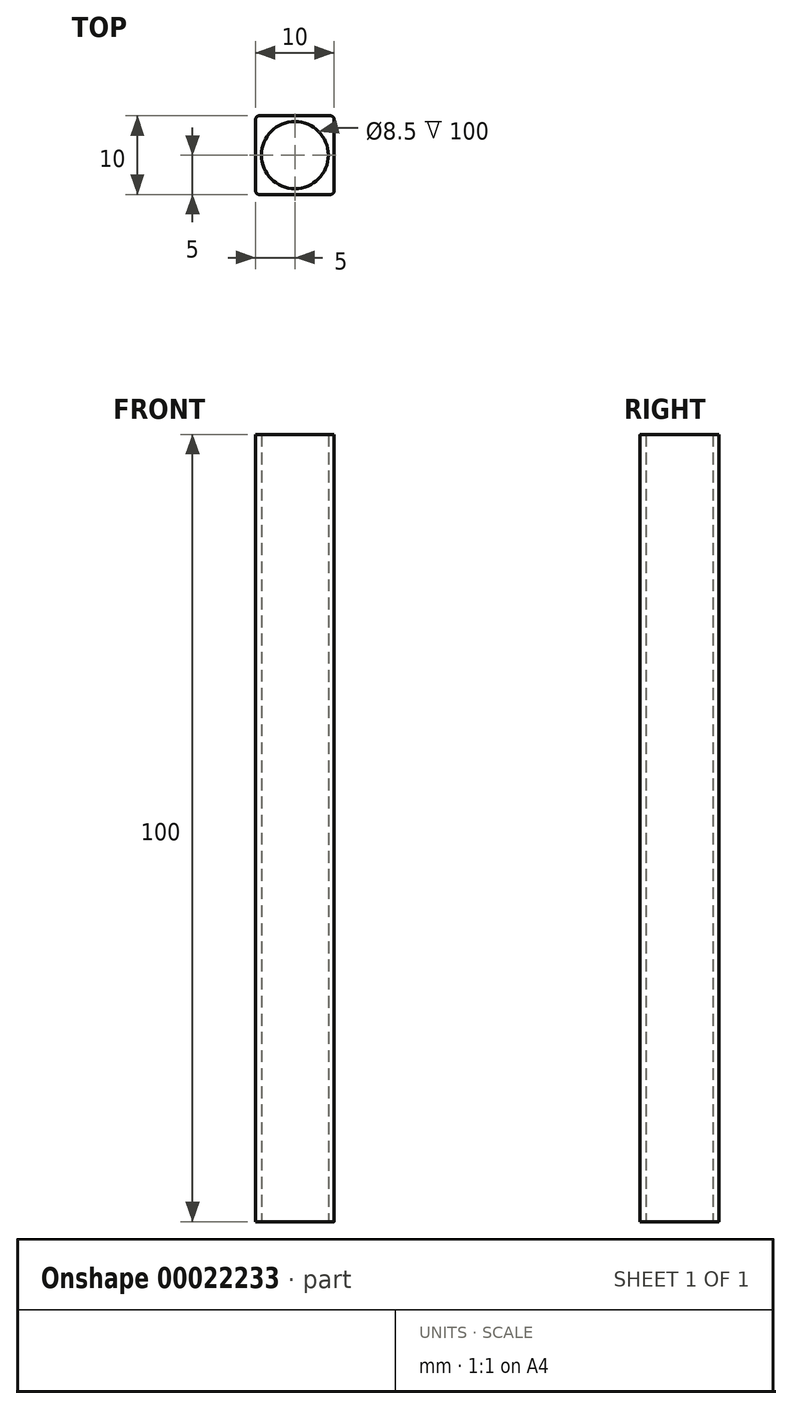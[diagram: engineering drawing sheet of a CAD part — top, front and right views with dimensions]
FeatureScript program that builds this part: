
annotation { "Feature Type Name" : "Feature", "Feature Type Description" : "" }
export const myFeature = defineFeature(function(context is Context, id is Id, definition is map)
    precondition{}
    {
        {
            var Q0;
            Q0=qCreatedBy(makeId("Top.planeOp"),FACE);
            var sketch = newSketch(context, id + "F0", { "sketchPlane" : qUnion([Q0])});
            skLineSegment(sketch, "E0.rect.bottom", {"start": v(-4.5, 5) * mm, "end": v(4.5, 5) * mm});
            skLineSegment(sketch, "E0.rect.top", {"start": v(-4.5, -5) * mm, "end": v(4.5, -5) * mm});
            skLineSegment(sketch, "E0.rect.left", {"start": v(-5, 4.5) * mm, "end": v(-5, -4.5) * mm});
            skLineSegment(sketch, "E0.rect.right", {"start": v(5, 4.5) * mm, "end": v(5, -4.5) * mm});
            skPoint(sketch, "E0.rect.middle", {"position": v(0, 0) * mm});
            skCircle(sketch, "E1", {"center": v(0, 0) * mm, "radius": 4.25 * mm});
            skPoint(sketch, "E2.visualSharp", {"position": v(-5, 5) * mm});
            skArc(sketch, "E2.filletArc", {"start": v(-4.5, 5) * mm, "mid": v(-4.85, 4.85) * mm, "end": v(-5, 4.5) * mm});
            skPoint(sketch, "E3.visualSharp", {"position": v(-5, -5) * mm});
            skArc(sketch, "E3.filletArc", {"start": v(-5, -4.5) * mm, "mid": v(-4.85, -4.85) * mm, "end": v(-4.5, -5) * mm});
            skPoint(sketch, "E4.visualSharp", {"position": v(5, -5) * mm});
            skArc(sketch, "E4.filletArc", {"start": v(4.5, -5) * mm, "mid": v(4.85, -4.85) * mm, "end": v(5, -4.5) * mm});
            skPoint(sketch, "E5.visualSharp", {"position": v(5, 5) * mm});
            skArc(sketch, "E5.filletArc", {"start": v(5, 4.5) * mm, "mid": v(4.85, 4.85) * mm, "end": v(4.5, 5) * mm});
            skSolve(sketch);
        }
        {
            var Q0;
            Q0 = qSketchRegion(id + "F0", true);
            extrude(context, id + "F1", {"entities" : qUnion([Q0]), "depth" : 100 * mm});
        }
    });
